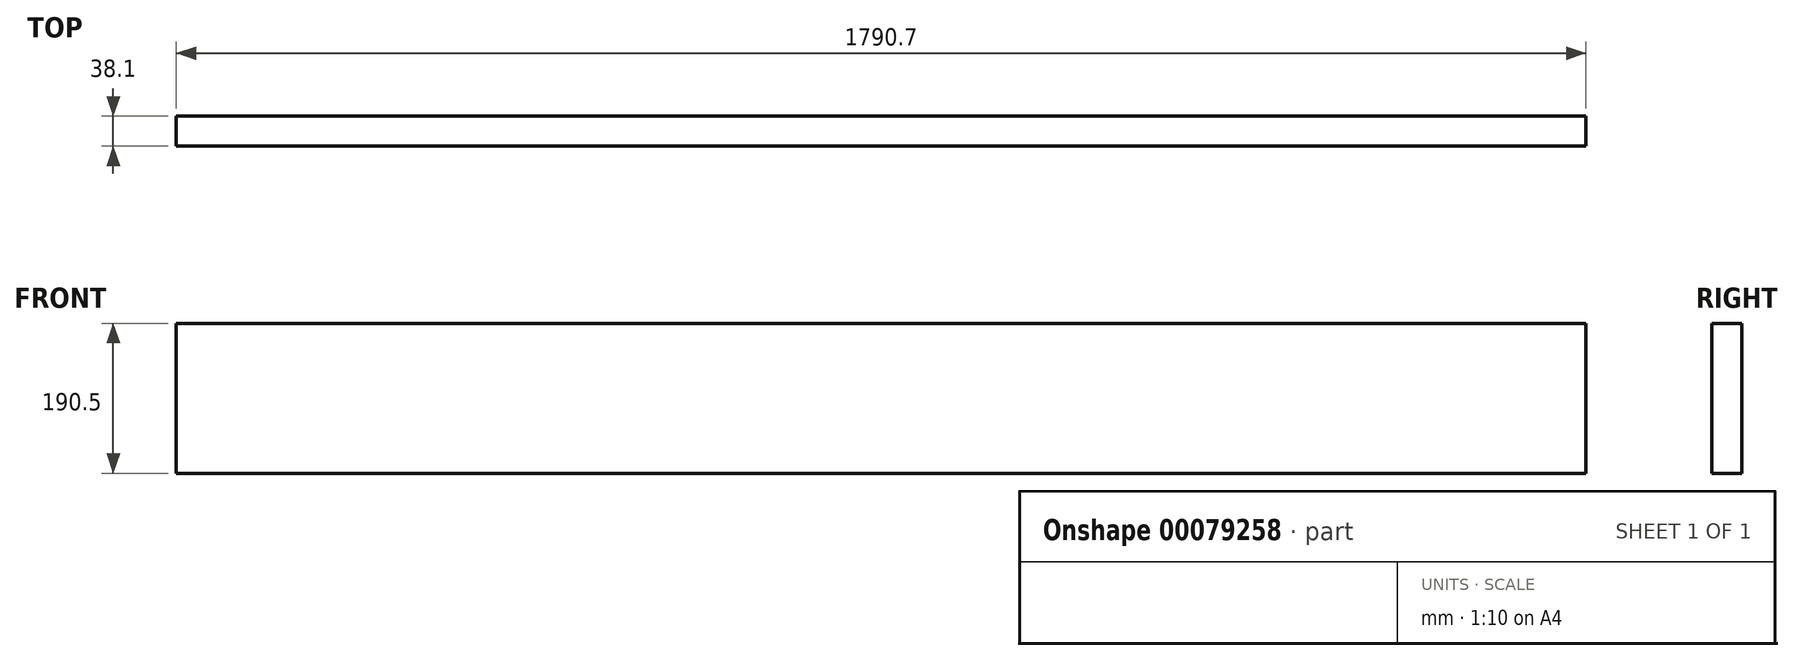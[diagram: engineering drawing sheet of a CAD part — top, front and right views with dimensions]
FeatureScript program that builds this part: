
annotation { "Feature Type Name" : "Feature", "Feature Type Description" : "" }
export const myFeature = defineFeature(function(context is Context, id is Id, definition is map)
    precondition{}
    {
        {
            var Q0;
            Q0=qCreatedBy(makeId("Right.planeOp"),FACE);
            var sketch = newSketch(context, id + "F0", { "sketchPlane" : qUnion([Q0])});
            skLineSegment(sketch, "E0.bottom", {"start": v(0, 0) * mm, "end": v(-38.1, 0) * mm});
            skLineSegment(sketch, "E0.top", {"start": v(0, 190.5) * mm, "end": v(-38.1, 190.5) * mm});
            skLineSegment(sketch, "E0.left", {"start": v(0, 0) * mm, "end": v(0, 190.5) * mm});
            skLineSegment(sketch, "E0.right", {"start": v(-38.1, 0) * mm, "end": v(-38.1, 190.5) * mm});
            skSolve(sketch);
        }
        {
            var Q0;
            Q0=makeQuery(id+"F0.imprint","IMPRINT",FACE,{"disambiguationData":[TD([[makeQuery(id+"F0.imprint","IMPRINT",EDGE,{"derivedFrom":sQuery(id+"F0.wireOp",EDGE,"E0.bottom")}),-1.0]])]});
            extrude(context, id + "F1", {"entities" : qUnion([Q0]), "depth" : 1790.7 * mm});
        }
    });
